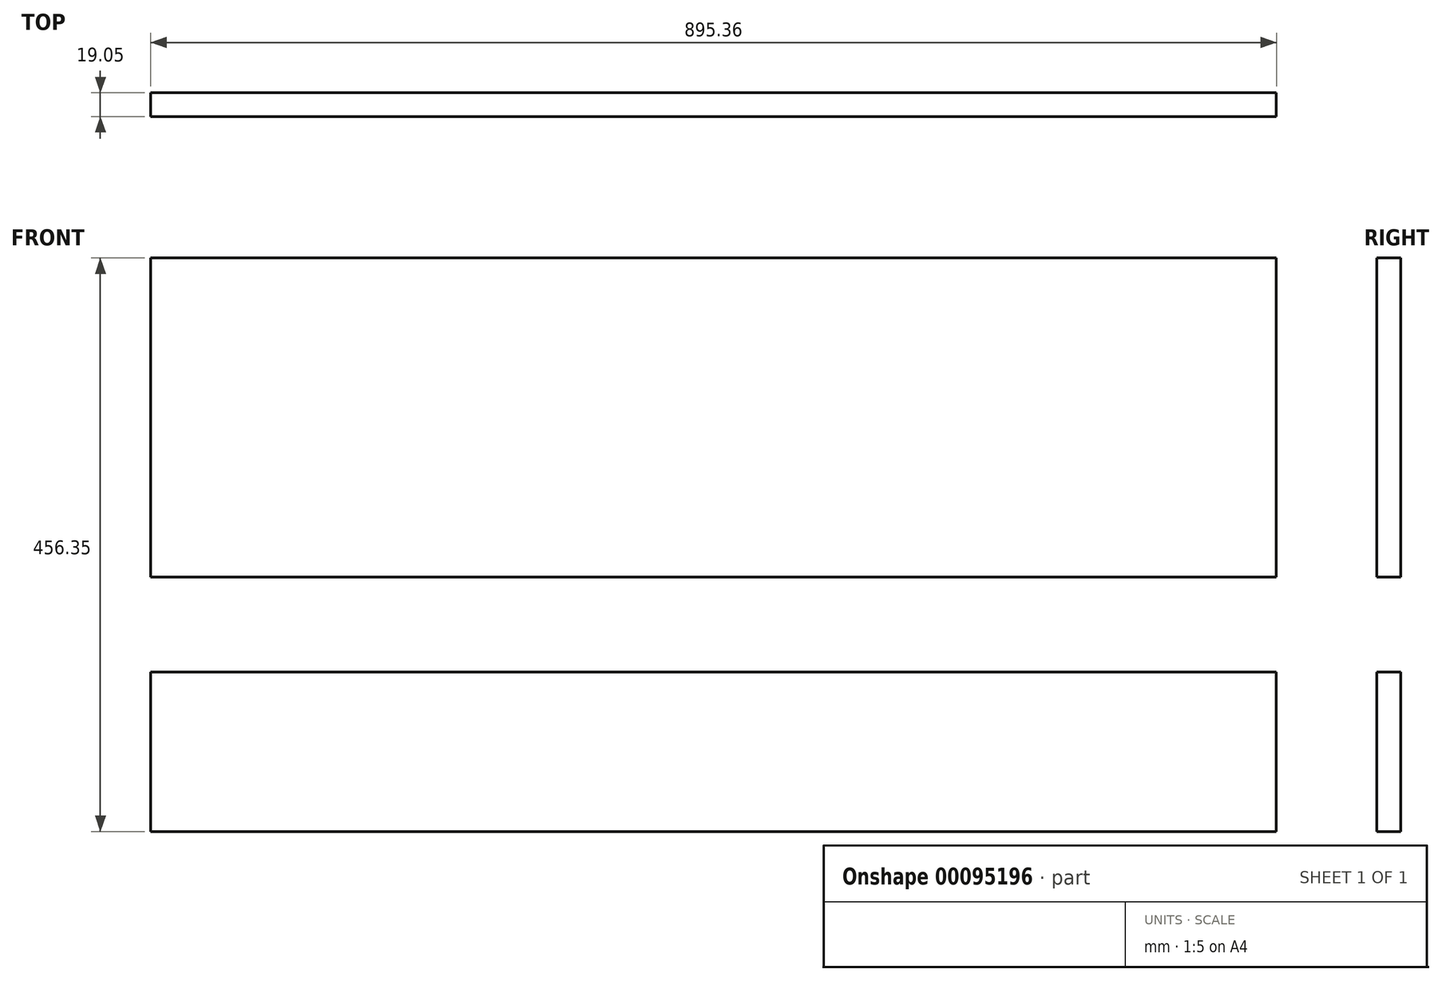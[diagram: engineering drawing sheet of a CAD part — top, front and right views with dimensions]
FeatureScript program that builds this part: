
annotation { "Feature Type Name" : "Feature", "Feature Type Description" : "" }
export const myFeature = defineFeature(function(context is Context, id is Id, definition is map)
    precondition{}
    {
        {
            var Q0;
            Q0=qCreatedBy(makeId("Front.planeOp"),FACE);
            var sketch = newSketch(context, id + "F0", { "sketchPlane" : qUnion([Q0])});
            skLineSegment(sketch, "E0.bottom", {"start": v(-447.68, -63.5) * mm, "end": v(447.68, -63.5) * mm});
            skLineSegment(sketch, "E0.top", {"start": v(-447.68, 63.5) * mm, "end": v(447.68, 63.5) * mm});
            skLineSegment(sketch, "E0.left", {"start": v(-447.68, -63.5) * mm, "end": v(-447.68, 63.5) * mm});
            skLineSegment(sketch, "E0.right", {"start": v(447.68, -63.5) * mm, "end": v(447.68, 63.5) * mm});
            skPoint(sketch, "E0.middle", {"position": v(0, 0) * mm});
            skLineSegment(sketch, "E1.bottom", {"start": v(-447.68, 138.85) * mm, "end": v(447.68, 138.85) * mm});
            skLineSegment(sketch, "E1.top", {"start": v(-447.68, 392.85) * mm, "end": v(447.67, 392.85) * mm});
            skLineSegment(sketch, "E1.left", {"start": v(-447.68, 138.85) * mm, "end": v(-447.68, 392.85) * mm});
            skLineSegment(sketch, "E1.right", {"start": v(447.68, 138.85) * mm, "end": v(447.68, 392.85) * mm});
            skSolve(sketch);
        }
        {
            var Q0;
            Q0=makeQuery(id+"F0.imprint","IMPRINT",FACE,{"disambiguationData":[TD([[makeQuery(id+"F0.imprint","IMPRINT",EDGE,{"derivedFrom":sQuery(id+"F0.wireOp",EDGE,"E1.bottom")}),1.0]])]});
            var Q1;
            Q1=makeQuery(id+"F0.imprint","IMPRINT",FACE,{"disambiguationData":[TD([[makeQuery(id+"F0.imprint","IMPRINT",EDGE,{"derivedFrom":sQuery(id+"F0.wireOp",EDGE,"E0.bottom")}),1.0]])]});
            extrude(context, id + "F1", {"entities" : qUnion([Q0, Q1]), "depth" : 19.05 * mm});
        }
    });
